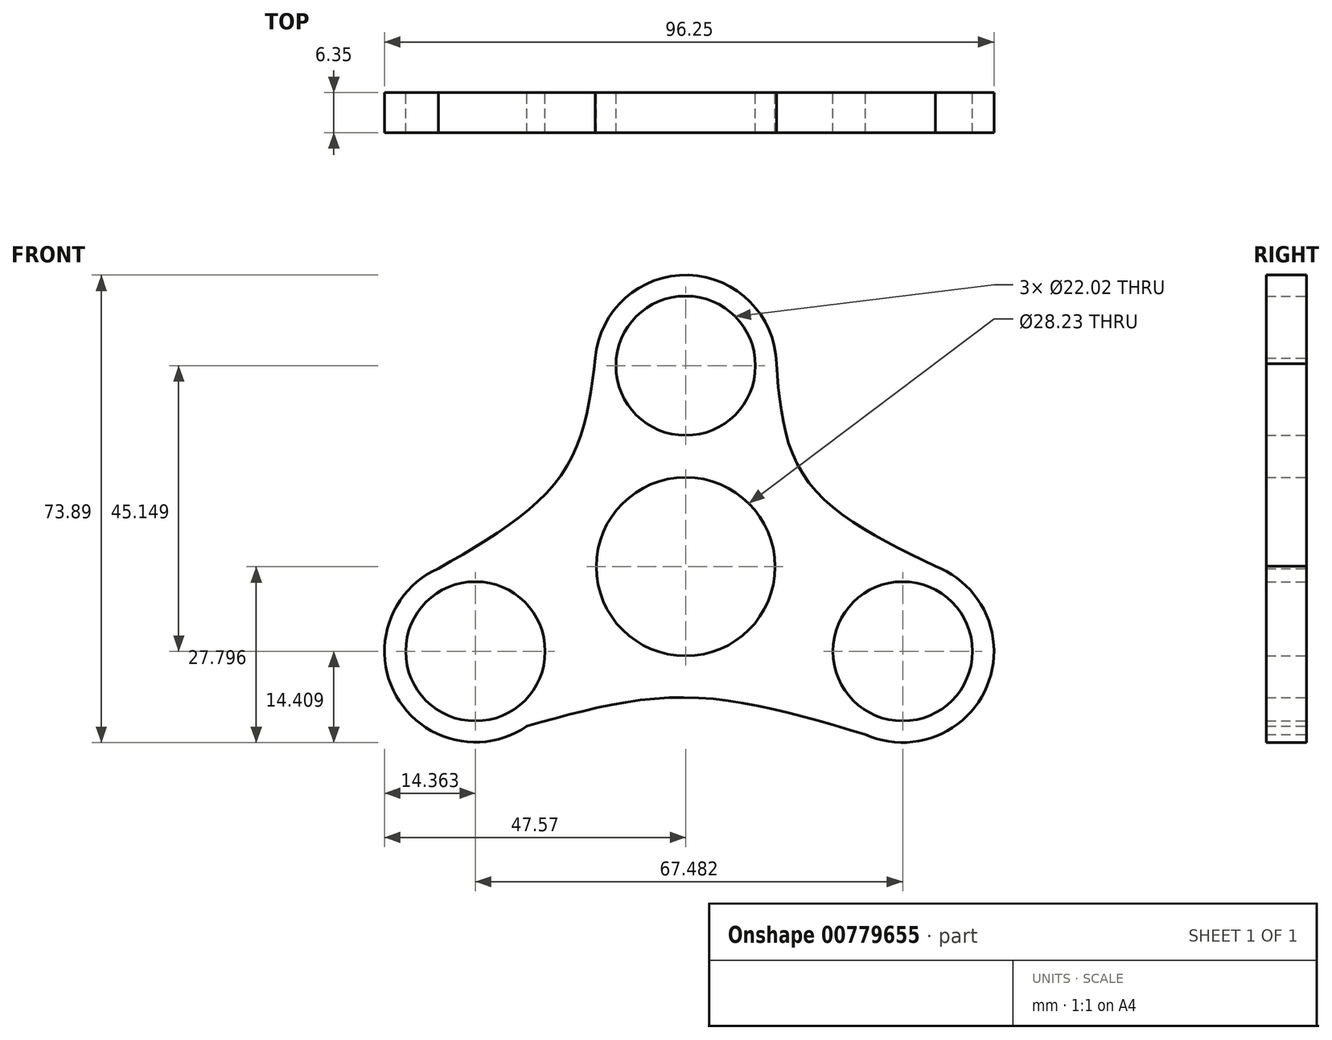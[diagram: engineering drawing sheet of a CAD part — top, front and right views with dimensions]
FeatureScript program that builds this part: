
annotation { "Feature Type Name" : "Feature", "Feature Type Description" : "" }
export const myFeature = defineFeature(function(context is Context, id is Id, definition is map)
    precondition{}
    {
        {
            var Q0;
            Q0=qCreatedBy(makeId("Front.planeOp"),FACE);
            var sketch = newSketch(context, id + "F0", { "sketchPlane" : qUnion([Q0])});
            skCircle(sketch, "E0", {"center": v(0, 43.26) * mm, "radius": 11.01 * mm});
            skCircle(sketch, "E1", {"center": v(0, 11.5) * mm, "radius": 11.01 * mm});
            skCircle(sketch, "E2", {"center": v(34.27, -1.9) * mm, "radius": 11.01 * mm});
            skCircle(sketch, "E3", {"center": v(-33.2, -1.9) * mm, "radius": 11.01 * mm});
            skCircle(sketch, "E4", {"center": v(0, 43.26) * mm, "radius": 14.34 * mm});
            skCircle(sketch, "E5", {"center": v(-33.2, -1.9) * mm, "radius": 14.36 * mm});
            skCircle(sketch, "E6", {"center": v(34.27, -1.9) * mm, "radius": 14.4 * mm});
            skCircle(sketch, "E7", {"center": v(0, 11.5) * mm, "radius": 14.12 * mm});
            skFitSpline(sketch, "E8", {"points": [v(-14.19, 45.3) * mm, v(-19.57, 26.1) * mm, v(-41.3, 9.97) * mm], "startDerivative": vector(-5.04, -44.26) * mm, "endDerivative": vector(-48.13, -26.84) * mm});
            skFitSpline(sketch, "E9", {"points": [v(-25.07, -13.72) * mm, v(0, -9.17) * mm, v(28.37, -15.03) * mm], "startDerivative": vector(51.04, 14.46) * mm, "endDerivative": vector(55.8, -16.76) * mm});
            skFitSpline(sketch, "E10", {"points": [v(14.24, 44.94) * mm, v(18.93, 25.49) * mm, v(39.43, 11.56) * mm], "startDerivative": vector(3.09, -44.56) * mm, "endDerivative": vector(46.56, -22.55) * mm});
            skSolve(sketch);
        }
        {
            var Q0;
            Q0 = qSketchRegion(id + "F0", true);
            extrude(context, id + "F1", {"entities" : qUnion([Q0]), "depth" : 6.35 * mm, "offsetDistance" : 25.4 * mm});
        }
    });
